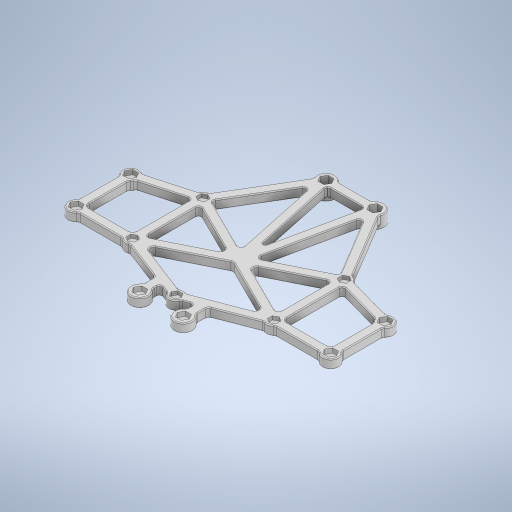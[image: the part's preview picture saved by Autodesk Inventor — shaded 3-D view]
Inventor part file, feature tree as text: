
AUTODESK INVENTOR PART (.ipt)
format: ipt  version: 2024.2 (Build 282272000, 272)  size: 1,422,336 bytes
history: native  units: mm
features: projected_geometry x67, extrude x8, sketch x6, fillet x5, hole x2
ambient origin geometry x8: Origin, YZ Plane, XZ Plane, XY Plane, X Axis, Y Axis, Z Axis, Center Point
bodies: Solid1 (feature_tree)
feature tree (88):
  sketch  "Sketch1"  dims[d0=4.8mm d9=5.6mm]
  extrude  "Extrusion1"  Depth=5.6mm
  sketch  "Sketch2"  dims[d10=30.0mm d11=9.0mm]
  extrude  "Extrusion2"  Depth=9.0mm
  extrude  "Extrusion3"  Depth=5.0mm
  extrude  "Extrusion4"  Depth=2.5mm
  extrude  "Extrusion5"  Depth=2.5mm
  hole  "Hole1"  [1 undecoded]
  hole  "Hole2"  [1 undecoded]
  fillet  "Fillet1"  Radius=2.5mm
  fillet  "Fillet2"  Radius=2.5mm
  fillet  "Fillet3"  Radius=5.0mm
  fillet  "Fillet7"  Radius=2.5mm
  fillet  "Fillet8"  Radius=5.0mm
  extrude  "Extrusion6"  Depth=2.5mm
  extrude  "Extrusion7"  Depth=2.5mm
  extrude  "Extrusion8"  Depth=2.5mm
  projected_geometry  "Projected Loop1"
  projected_geometry  "Projected Loop2"
  projected_geometry  "Projected Loop3"
  projected_geometry  "Projected Loop4"
  projected_geometry  "Projected Loop5"
  projected_geometry  "Projected Loop6"
  projected_geometry  "Projected Loop7"
  projected_geometry  "Projected Loop8"
  projected_geometry  "Projected Loop9"
  projected_geometry  "Projected Loop10"
  projected_geometry  "Projected Loop11"
  projected_geometry  "Projected Loop12"
  projected_geometry  "Projected Loop13"
  projected_geometry  "Projected Loop14"
  projected_geometry  "Projected Loop15"
  projected_geometry  "Projected Loop16"
  projected_geometry  "Projected Loop17"
  projected_geometry  "Projected Loop18"
  projected_geometry  "Projected Loop19"
  projected_geometry  "Projected Loop20"
  projected_geometry  "Projected Loop21"
  projected_geometry  "Projected Loop22"
  projected_geometry  "Projected Loop23"
  projected_geometry  "Projected Loop24"
  projected_geometry  "Projected Loop25"
  projected_geometry  "Projected Loop26"
  projected_geometry  "Projected Loop27"
  projected_geometry  "Projected Loop28"
  projected_geometry  "Projected Loop29"
  projected_geometry  "Projected Loop30"
  projected_geometry  "Projected Loop31"
  projected_geometry  "Projected Loop32"
  projected_geometry  "Projected Loop33"
  projected_geometry  "Projected Loop34"
  projected_geometry  "Projected Loop35"
  projected_geometry  "Projected Loop36"
  projected_geometry  "Projected Loop37"
  projected_geometry  "Projected Loop38"
  projected_geometry  "Projected Loop39"
  projected_geometry  "Projected Loop40"
  projected_geometry  "Projected Loop41"
  projected_geometry  "Projected Loop42"
  projected_geometry  "Projected Loop43"
  projected_geometry  "Projected Loop44"
  projected_geometry  "Projected Loop45"
  projected_geometry  "Projected Loop46"
  projected_geometry  "Projected Loop47"
  projected_geometry  "Projected Loop48"
  projected_geometry  "Projected Loop49"
  projected_geometry  "Projected Loop50"
  projected_geometry  "Projected Loop51"
  projected_geometry  "Projected Loop52"
  projected_geometry  "Projected Loop53"
  projected_geometry  "Projected Loop54"
  projected_geometry  "Projected Loop55"
  projected_geometry  "Projected Loop56"
  projected_geometry  "Projected Loop57"
  projected_geometry  "Projected Loop58"
  projected_geometry  "Projected Loop59"
  projected_geometry  "Projected Loop60"
  projected_geometry  "Projected Loop61"
  projected_geometry  "Projected Loop62"
  projected_geometry  "Projected Loop63"
  projected_geometry  "Projected Loop64"
  projected_geometry  "Projected Loop65"
  projected_geometry  "Projected Loop66"
  projected_geometry  "Projected Loop67"
  sketch  "Sketch3"  dims[d16=140.0mm d17=5.0mm]
  sketch  "Sketch4"  dims[d18=2.5mm d22=5.0mm]
  sketch  "Sketch6"  dims[d23=2.5mm d24=2.5mm]
  sketch  "Sketch7"  dims[d25=2.5mm d26=2.5mm d27=5.0mm d28=2.5mm d29=2.5mm d30=5.0mm d31=2.5mm d32=5.0mm d33=2.5mm d34=2.5mm d35=2.5mm d36=5.0mm d37=2.5mm d42=27.0mm d48=2.5mm d51=12.0mm d52=8.0mm d53=10.0mm d55=8.0mm d56=5.0mm d57=2.5mm d58=24.0mm d59=5.0mm d60=0.0mm d61=1.9mm d62=0.0mm d63=2.5mm d64=0.0mm d65=3.5mm d66=6.0mm d67=4.0mm d68=2.0mm d69=90.0deg d70=6.0mm d71=0.0mm d72=5.25mm d73=6.0mm d74=4.0mm d75=2.0mm d76=90.0deg d77=1.0mm d78=0.0mm d79=5.0mm d80=0.0mm d81=2.0mm d82=2.0mm d83=1.5mm d90=96.0mm d91=5.0mm d92=2.5mm d95=2.5mm d96=2.5mm d97=2.5mm d98=5.0mm d100=2.0mm d101=0.0mm d102=5.0mm d103=15.0mm d104=2.5mm d105=2.5mm d106=2.5mm d107=5.0mm d108=5.0mm d109=2.5mm d110=42.0mm d127=73.0mm d129=0.2mm d130=0.0mm d131=0.2mm d132=0.0mm d133=0.2mm d134=0.0mm d135=5.0mm d136=2.5mm d137=5.0mm d138=2.5mm d139=8.0mm d140=1.0mm d141=0.5mm d142=70.0mm d84=0.0mm d85=0.0mm d86=0.0mm d87=0.0mm]
note: 2 required parameter values undecoded (feature->parameter linkage not recoverable at this tier; creation-order binding heuristic only, values carry confidence <= 0.55)
